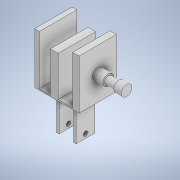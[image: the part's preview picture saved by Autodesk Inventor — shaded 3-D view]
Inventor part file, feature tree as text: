
AUTODESK INVENTOR PART (.ipt)
format: ipt  version: 2021 (Build 250183000, 183)  size: 174,080 bytes
history: native  units: mm
features: extrude x6, sketch x6
ambient origin geometry x8: Origin, YZ Plane, XZ Plane, XY Plane, X Axis, Y Axis, Z Axis, Center Point
bodies: Solid1 (feature_tree)
feature tree (12):
  extrude  "Extrusion1"  TaperAngle=0.0deg  [1 undecoded]
  extrude  "Extrusion2"  Depth=35.0mm TaperAngle=0.0deg
  extrude  "Extrusion3"  Depth=35.0mm
  extrude  "Extrusion4"  TaperAngle=0.0deg  [1 undecoded]
  extrude  "Extrusion5"  [1 undecoded]
  extrude  "Extrusion6"  [1 undecoded]
  sketch  "Sketch1"  dims[d10=0.0mm d14=0.0mm]
  sketch  "Sketch2"  dims[d16=23.0mm d20=35.0mm d21=0.0mm]
  sketch  "Sketch3"  dims[d22=35.0mm d23=0.0mm d26=46.312mm]
  sketch  "Sketch4"  dims[d27=19.946mm d28=0.0mm d31=0.0mm]
  sketch  "Sketch5"  dims[d34=0.0mm]
  sketch  "Sketch6"
note: 4 required parameter values undecoded (feature->parameter linkage not recoverable at this tier; creation-order binding heuristic only, values carry confidence <= 0.55)
